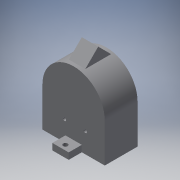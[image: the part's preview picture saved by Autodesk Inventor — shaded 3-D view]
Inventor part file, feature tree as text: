
AUTODESK INVENTOR PART (.ipt)
format: ipt  version: 2016 (Build 200138000, 138)  size: 156,672 bytes
history: native  units: in
note: dims shown in document units (in); Inventor stores cm internally (conversion verified against a paired STEP export)
features: extrude x7, sketch x6, reference x5, plane x1
ambient origin geometry x8: Origin, YZ Plane, XZ Plane, XY Plane, X Axis, Y Axis, Z Axis, Center Point
bodies: Solid1 (feature_tree)
feature tree (19):
  extrude  "Extrusion1"  Depth=0.197in
  extrude  "Extrusion2"  Depth=0.4in
  extrude  "Extrusion3"  Depth=0.4in TaperAngle=0.0deg
  extrude  "Extrusion4"  Depth=0.5in
  extrude  "Extrusion5"  Depth=0.4in TaperAngle=0.0deg
  plane  "Work Plane1"
  extrude  "Extrusion6"  Depth=1.0in
  extrude  "Extrusion7"  Depth=0.4in TaperAngle=0.0deg
  sketch  "Sketch1"  dims[d1=1.0in d2=0.0in d3=0.197in]
  reference  "Reference1"
  reference  "Reference2"
  sketch  "Sketch2"  dims[d4=0.4in d5=0.0in d6=0.15in]
  reference  "Reference3"
  sketch  "Sketch3"  dims[d7=0.1772in d8=0.4in d9=0.0in]
  sketch  "Sketch5"  dims[d10=0.25in d11=0.5in]
  sketch  "Sketch6"  dims[d12=0.197in d13=0.4in d14=0.0in]
  sketch  "Sketch7"  dims[d15=0.15in d16=0.1378in d17=0.4in d18=0.0in d19=0.5in d20=1.9in d21=-0.95in d22=0.1065in d23=0.787in d24=0.394in d25=0.394in d26=0.5in d27=0.0in d28=0.0394in d29=0.098in d30=0.0394in d31=0.098in d32=1.0in d33=0.0in]
  reference  "Reference4"
  reference  "Reference5"
